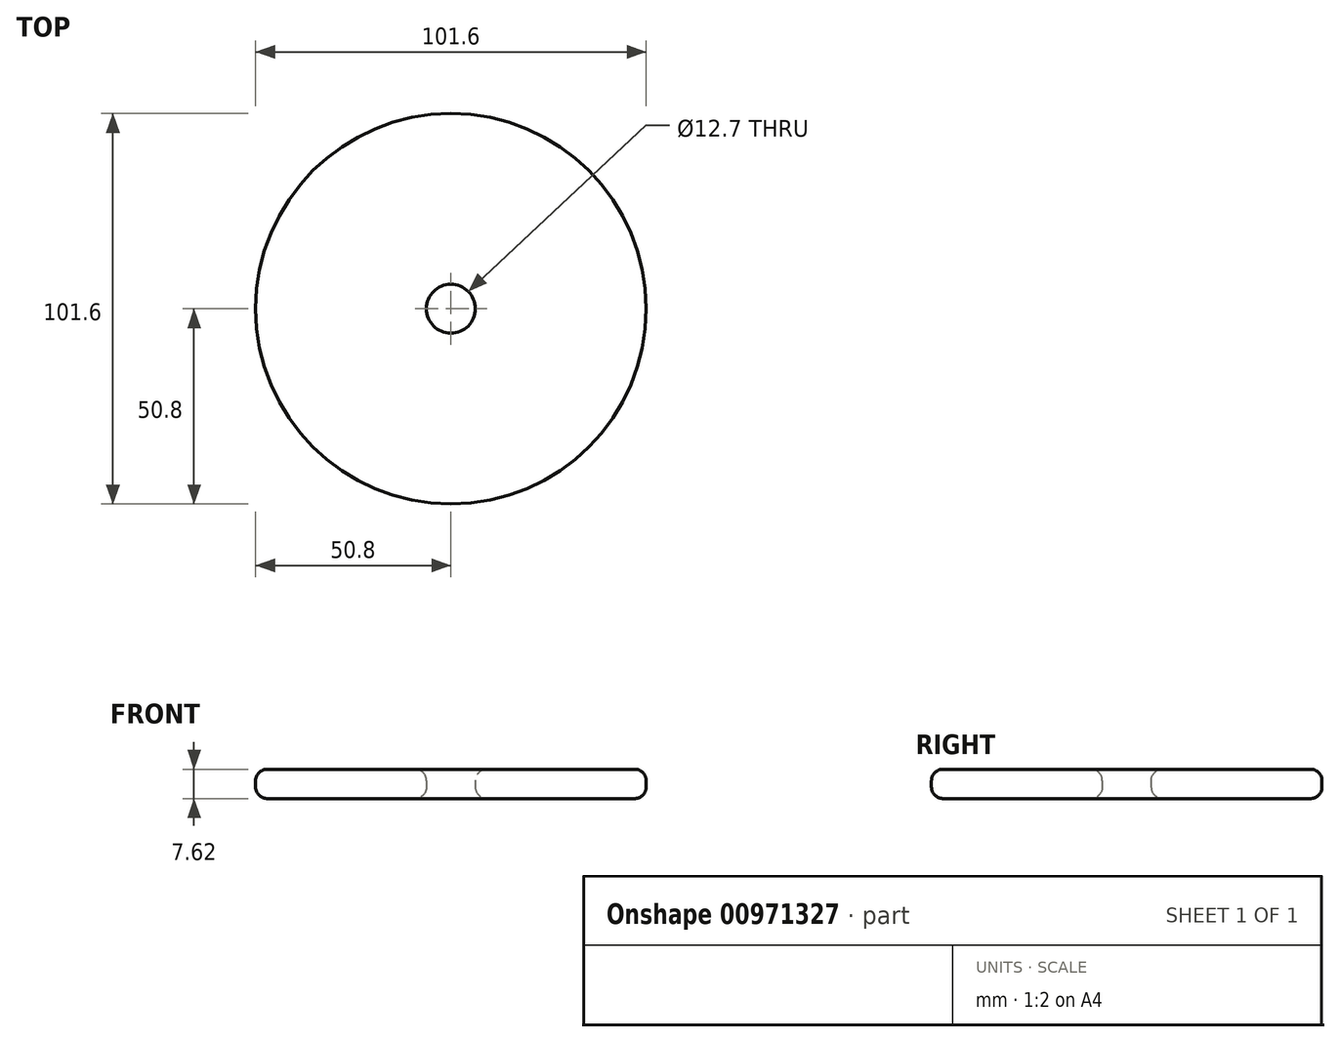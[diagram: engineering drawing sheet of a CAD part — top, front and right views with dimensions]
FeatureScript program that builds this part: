
annotation { "Feature Type Name" : "Feature", "Feature Type Description" : "" }
export const myFeature = defineFeature(function(context is Context, id is Id, definition is map)
    precondition{}
    {
        {
            var Q0;
            Q0=qCreatedBy(makeId("Top.planeOp"),FACE);
            var sketch = newSketch(context, id + "F0", { "sketchPlane" : qUnion([Q0])});
            skCircle(sketch, "E0", {"center": v(0, 0) * mm, "radius": 50.8 * mm});
            skCircle(sketch, "E1", {"center": v(0, 0) * mm, "radius": 6.35 * mm});
            skSolve(sketch);
        }
        {
            var Q0;
            Q0=makeQuery(id+"F0.imprint","IMPRINT",FACE,{"disambiguationData":[TD([[makeQuery(id+"F0.imprint","IMPRINT",EDGE,{"derivedFrom":sQuery(id+"F0.wireOp",EDGE,"E0")}),1.0]])]});
            extrude(context, id + "F1", {"entities" : qUnion([Q0]), "depth" : 7.62 * mm, "offsetDistance" : 25.4 * mm});
        }
        {
            var Q0;
            Q0=makeQuery(id+"F1.opExtrude","CAP_FACE",FACE,{"disambiguationData":[OSD([sQuery(id+"F0.wireOp",EDGE,"E0"),sQuery(id+"F0.wireOp",EDGE,"E1")])],"isStart":false});
            var Q1;
            Q1=makeQuery(id+"F1.opExtrude","CAP_FACE",FACE,{"disambiguationData":[OSD([sQuery(id+"F0.wireOp",EDGE,"E0"),sQuery(id+"F0.wireOp",EDGE,"E1")])],"isStart":true});
            fillet(context, id + "F2", {"entities" : qUnion([Q0, Q1]), "radius" : 3 * mm, "tangentPropagation" : true, "allowEdgeOverflow" : false});
        }
        {
            var Q0;
            Q0=qCreatedBy(makeId("Top.planeOp"),FACE);
            cPlane(context, id + "F3", {"entities" : qUnion([Q0]), "cplaneType" : CPlaneType.OFFSET, "offset" : 7.87 * mm, "oppositeDirection" : true, "width" : 152.4 * mm, "height" : 152.4 * mm});
        }
    });
